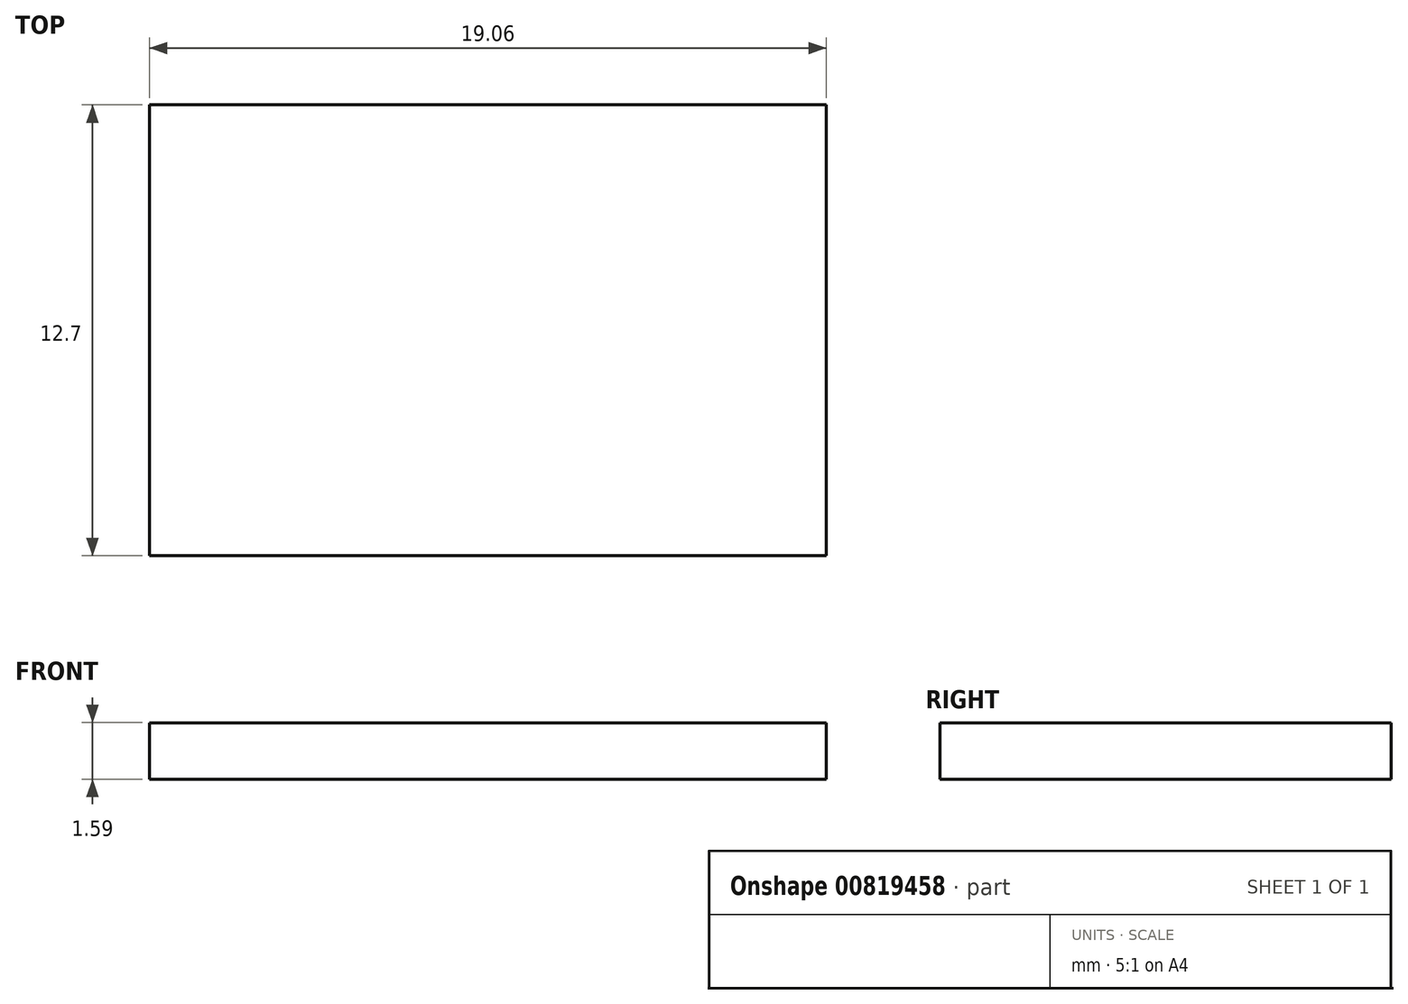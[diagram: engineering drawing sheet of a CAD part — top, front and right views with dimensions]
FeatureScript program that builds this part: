
annotation { "Feature Type Name" : "Feature", "Feature Type Description" : "" }
export const myFeature = defineFeature(function(context is Context, id is Id, definition is map)
    precondition{}
    {
        {
            var Q0;
            Q0=qCreatedBy(makeId("Top.planeOp"),FACE);
            var sketch = newSketch(context, id + "F0", { "sketchPlane" : qUnion([Q0])});
            skLineSegment(sketch, "E0.bottom", {"start": v(9.53, -6.35) * mm, "end": v(-9.53, -6.35) * mm});
            skLineSegment(sketch, "E0.top", {"start": v(9.53, 6.35) * mm, "end": v(-9.53, 6.35) * mm});
            skLineSegment(sketch, "E0.left", {"start": v(9.53, -6.35) * mm, "end": v(9.53, 6.35) * mm});
            skLineSegment(sketch, "E0.right", {"start": v(-9.53, -6.35) * mm, "end": v(-9.53, 6.35) * mm});
            skPoint(sketch, "E0.middle", {"position": v(0, 0) * mm});
            skSolve(sketch);
        }
        {
            var Q0;
            Q0 = qSketchRegion(id + "F0", true);
            extrude(context, id + "F1", {"entities" : qUnion([Q0]), "depth" : 1.59 * mm, "offsetDistance" : 25.4 * mm});
        }
    });
